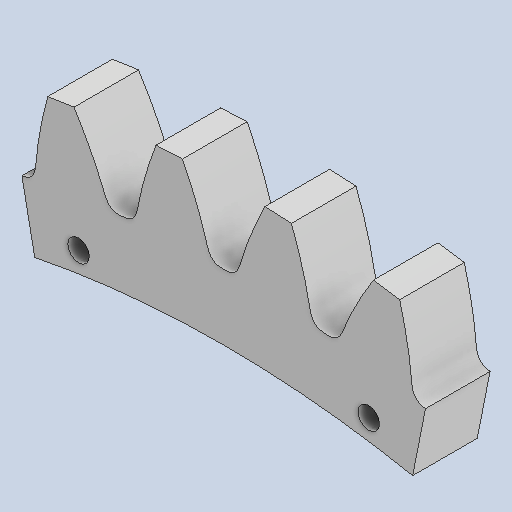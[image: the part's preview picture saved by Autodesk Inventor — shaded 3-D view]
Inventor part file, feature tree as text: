
AUTODESK INVENTOR PART (.ipt)
format: ipt  version: 2025 (Build 290162010, 162A)  size: 437,248 bytes
history: native  units: mm
features: extrude x3, sketch x2, pattern_circular x1, hole x1, projected_geometry x1
ambient origin geometry x8: Origin, YZ Plane, XZ Plane, XY Plane, X Axis, Y Axis, Z Axis, Center Point
bodies: Solid1 (feature_tree)
feature tree (8):
  extrude  "Extrusion1"  TaperAngle=0.0deg  [1 undecoded]
  extrude  "Extrusion2"  Depth=4.0mm
  pattern_circular  "Circular Pattern1"  Count=72  [1 undecoded]
  extrude  "Extrusion3"  TaperAngle=0.0deg  [1 undecoded]
  hole  "Hole1"  [1 undecoded]
  sketch  "Sketch2"  dims[d0=24.0mm d1=0.0mm d2=0.0mm d3=0.0mm]
  projected_geometry  "Projected Loop1"
  sketch  "Sketch3"  dims[d4=640.0mm d5=360.0deg d7=768.749998mm d8=720.0mm d10=0.0mm d11=0.0mm d12=22.5deg d13=735.0mm d14=1.472622mm d15=1.472622mm d16=8.0mm d17=6.0mm d18=4.0mm d19=2.0mm d20=90.0deg d21=8.0mm d22=20.594885mm]
note: 4 required parameter values undecoded (feature->parameter linkage not recoverable at this tier; creation-order binding heuristic only, values carry confidence <= 0.55)
